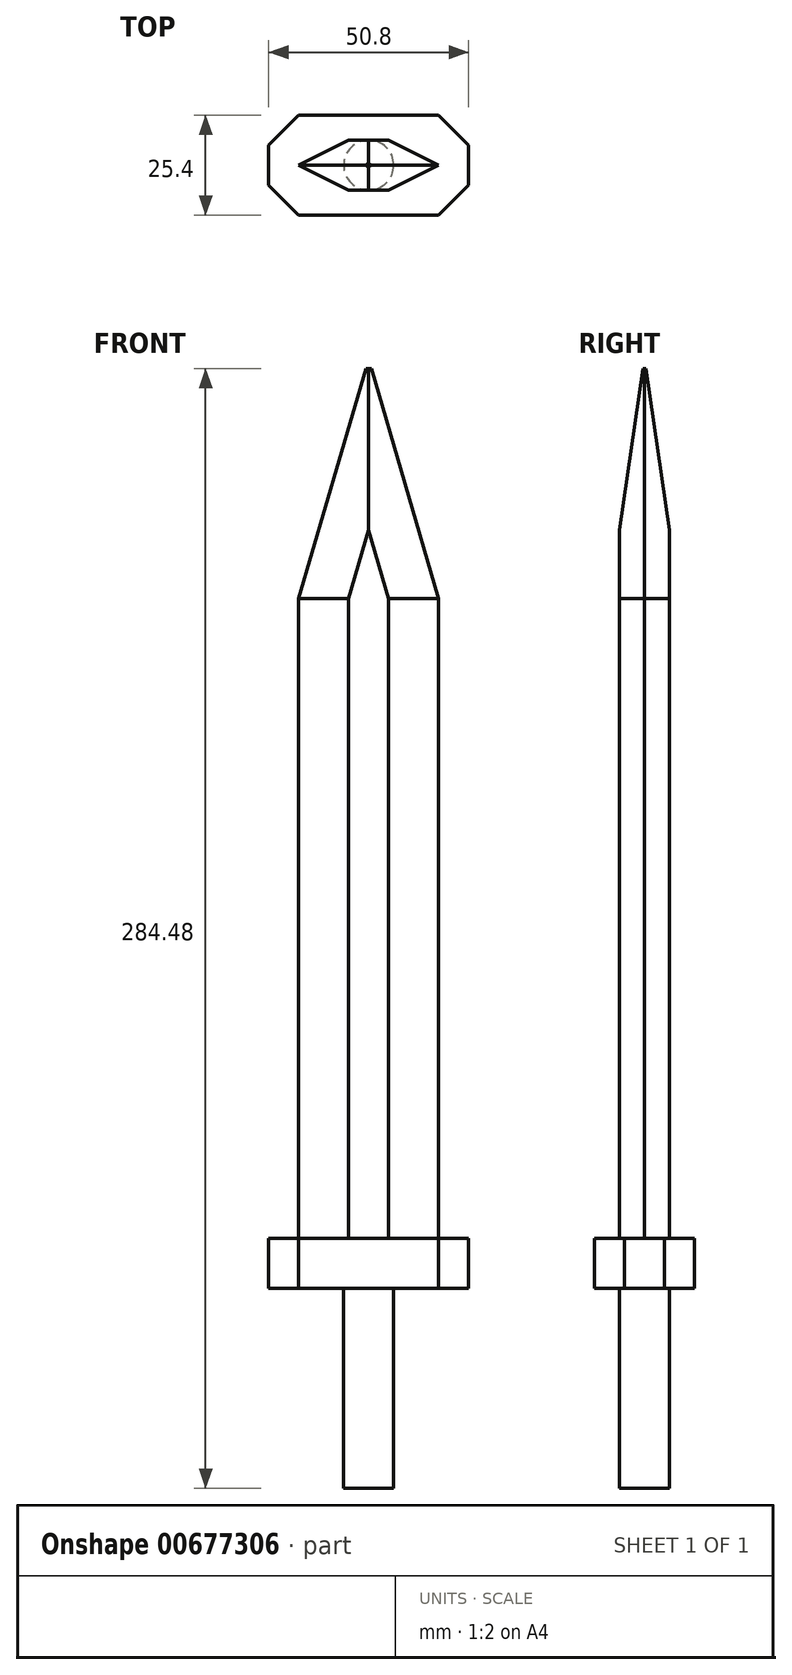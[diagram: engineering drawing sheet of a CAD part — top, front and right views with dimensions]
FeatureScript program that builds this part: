
annotation { "Feature Type Name" : "Feature", "Feature Type Description" : "" }
export const myFeature = defineFeature(function(context is Context, id is Id, definition is map)
    precondition{}
    {
        {
            var Q0;
            Q0=qCreatedBy(makeId("Top.planeOp"),FACE);
            var sketch = newSketch(context, id + "F0", { "sketchPlane" : qUnion([Q0])});
            skLineSegment(sketch, "E0.bottom", {"start": v(-25.4, 12.7) * mm, "end": v(25.4, 12.7) * mm});
            skLineSegment(sketch, "E0.top", {"start": v(-25.4, -12.7) * mm, "end": v(25.4, -12.7) * mm});
            skLineSegment(sketch, "E0.left", {"start": v(-25.4, 12.7) * mm, "end": v(-25.4, -12.7) * mm});
            skLineSegment(sketch, "E0.right", {"start": v(25.4, 12.7) * mm, "end": v(25.4, -12.7) * mm});
            skSolve(sketch);
        }
        {
            var Q0;
            Q0 = qSketchRegion(id + "F0", true);
            extrude(context, id + "F1", {"entities" : qUnion([Q0]), "depth" : 12.7 * mm, "offsetDistance" : 25.4 * mm});
        }
        {
            var Q0;
            Q0=makeQuery(id+"F1.opExtrude","CAP_FACE",FACE,{"disambiguationData":[OSD([sQuery(id+"F0.wireOp",EDGE,"E0.bottom"),sQuery(id+"F0.wireOp",EDGE,"E0.top"),sQuery(id+"F0.wireOp",EDGE,"E0.left"),sQuery(id+"F0.wireOp",EDGE,"E0.right")])],"isStart":true});
            var sketch = newSketch(context, id + "F2", { "sketchPlane" : qUnion([Q0])});
            skCircle(sketch, "E1", {"center": v(0, 0) * mm, "radius": 6.35 * mm});
            skSolve(sketch);
        }
        {
            var Q0;
            Q0=makeQuery(id+"F2.imprint","IMPRINT",FACE,{"disambiguationData":[TD([[makeQuery(id+"F2.imprint","IMPRINT",EDGE,{"derivedFrom":sQuery(id+"F2.wireOp",EDGE,"E1")}),1.0]])]});
            extrude(context, id + "F3", {"entities" : qUnion([Q0]), "operationType" : NewBodyOperationType.ADD, "depth" : 50.8 * mm, "offsetDistance" : 25.4 * mm});
        }
        {
            var Q0;
            Q0=makeQuery(id+"F1.opExtrude","CAP_FACE",FACE,{"disambiguationData":[OSD([sQuery(id+"F0.wireOp",EDGE,"E0.bottom"),sQuery(id+"F0.wireOp",EDGE,"E0.top"),sQuery(id+"F0.wireOp",EDGE,"E0.left"),sQuery(id+"F0.wireOp",EDGE,"E0.right")])],"isStart":false});
            var sketch = newSketch(context, id + "F4", { "sketchPlane" : qUnion([Q0])});
            skLineSegment(sketch, "E2.bottom", {"start": v(-17.78, -6.35) * mm, "end": v(17.78, -6.35) * mm});
            skLineSegment(sketch, "E2.top", {"start": v(-17.78, 6.35) * mm, "end": v(17.78, 6.35) * mm});
            skLineSegment(sketch, "E2.left", {"start": v(-17.78, -6.35) * mm, "end": v(-17.78, 6.35) * mm});
            skLineSegment(sketch, "E2.right", {"start": v(17.78, -6.35) * mm, "end": v(17.78, 6.35) * mm});
            skSolve(sketch);
        }
        {
            var Q0;
            Q0 = qSketchRegion(id + "F4", true);
            extrude(context, id + "F5", {"entities" : qUnion([Q0]), "operationType" : NewBodyOperationType.ADD, "depth" : 220.98 * mm, "offsetDistance" : 25.4 * mm});
        }
        {
            var Q0;
            Q0=makeQuery(id+"F5.opExtrude","SWEPT_EDGE",EDGE,{"disambiguationData":[OSD([sQuery(id+"F4.wireOp",EDGE,"E2.bottom"),sQuery(id+"F4.wireOp",EDGE,"E2.right")])]});
            var Q1;
            Q1=makeQuery(id+"F5.opExtrude","SWEPT_EDGE",EDGE,{"disambiguationData":[OSD([sQuery(id+"F4.wireOp",EDGE,"E2.top"),sQuery(id+"F4.wireOp",EDGE,"E2.right")])]});
            var Q2;
            Q2=makeQuery(id+"F5.opExtrude","SWEPT_EDGE",EDGE,{"disambiguationData":[OSD([sQuery(id+"F4.wireOp",EDGE,"E2.top"),sQuery(id+"F4.wireOp",EDGE,"E2.left")])]});
            var Q3;
            Q3=makeQuery(id+"F5.opExtrude","SWEPT_EDGE",EDGE,{"disambiguationData":[OSD([sQuery(id+"F4.wireOp",EDGE,"E2.bottom"),sQuery(id+"F4.wireOp",EDGE,"E2.left")])]});
            chamfer(context, id + "F6", {"entities" : qUnion([Q0, Q1, Q2, Q3]), "chamferType" : ChamferType.TWO_OFFSETS, "width1" : 6.35 * mm, "oppositeDirection" : false, "width2" : 12.7 * mm, "tangentPropagation" : true});
        }
        {
            var Q0;
            {var subQ0=sQuery(id+"F4.wireOp",EDGE,"E2.right");var subQ1=sQuery(id+"F4.wireOp",EDGE,"E2.top");Q0=makeQuery(id+"F6.opChamfer","BLEND_EDGE",EDGE,{"blendedFrom":[makeQuery(id+"F5.opExtrude","SWEPT_EDGE",EDGE,{"disambiguationData":[OSD([subQ1,subQ0])]}),makeQuery(id+"F5.opExtrude","CAP_FACE",FACE,{"disambiguationData":[OSD([sQuery(id+"F4.wireOp",EDGE,"E2.bottom"),subQ1,sQuery(id+"F4.wireOp",EDGE,"E2.left"),subQ0])],"isStart":false})],"blendedInto":[makeQuery(id+"F5.opExtrude","CAP_FACE",FACE,{"disambiguationData":[OSD([sQuery(id+"F4.wireOp",EDGE,"E2.bottom"),subQ1,sQuery(id+"F4.wireOp",EDGE,"E2.left"),subQ0])],"isStart":false})]});}
            var Q1;
            {var subQ0=sQuery(id+"F4.wireOp",EDGE,"E2.right");var subQ1=sQuery(id+"F4.wireOp",EDGE,"E2.bottom");Q1=makeQuery(id+"F6.opChamfer","BLEND_EDGE",EDGE,{"blendedFrom":[makeQuery(id+"F5.opExtrude","SWEPT_EDGE",EDGE,{"disambiguationData":[OSD([subQ1,subQ0])]}),makeQuery(id+"F5.opExtrude","CAP_FACE",FACE,{"disambiguationData":[OSD([subQ1,sQuery(id+"F4.wireOp",EDGE,"E2.top"),sQuery(id+"F4.wireOp",EDGE,"E2.left"),subQ0])],"isStart":false})],"blendedInto":[makeQuery(id+"F5.opExtrude","CAP_FACE",FACE,{"disambiguationData":[OSD([subQ1,sQuery(id+"F4.wireOp",EDGE,"E2.top"),sQuery(id+"F4.wireOp",EDGE,"E2.left"),subQ0])],"isStart":false})]});}
            var Q2;
            {var subQ0=sQuery(id+"F4.wireOp",EDGE,"E2.left");var subQ1=sQuery(id+"F4.wireOp",EDGE,"E2.bottom");Q2=makeQuery(id+"F6.opChamfer","BLEND_EDGE",EDGE,{"blendedFrom":[makeQuery(id+"F5.opExtrude","SWEPT_EDGE",EDGE,{"disambiguationData":[OSD([subQ1,subQ0])]}),makeQuery(id+"F5.opExtrude","CAP_FACE",FACE,{"disambiguationData":[OSD([subQ1,sQuery(id+"F4.wireOp",EDGE,"E2.top"),subQ0,sQuery(id+"F4.wireOp",EDGE,"E2.right")])],"isStart":false})],"blendedInto":[makeQuery(id+"F5.opExtrude","CAP_FACE",FACE,{"disambiguationData":[OSD([subQ1,sQuery(id+"F4.wireOp",EDGE,"E2.top"),subQ0,sQuery(id+"F4.wireOp",EDGE,"E2.right")])],"isStart":false})]});}
            var Q3;
            {var subQ0=sQuery(id+"F4.wireOp",EDGE,"E2.left");var subQ1=sQuery(id+"F4.wireOp",EDGE,"E2.top");Q3=makeQuery(id+"F6.opChamfer","BLEND_EDGE",EDGE,{"blendedFrom":[makeQuery(id+"F5.opExtrude","SWEPT_EDGE",EDGE,{"disambiguationData":[OSD([subQ1,subQ0])]}),makeQuery(id+"F5.opExtrude","CAP_FACE",FACE,{"disambiguationData":[OSD([sQuery(id+"F4.wireOp",EDGE,"E2.bottom"),subQ1,subQ0,sQuery(id+"F4.wireOp",EDGE,"E2.right")])],"isStart":false})],"blendedInto":[makeQuery(id+"F5.opExtrude","CAP_FACE",FACE,{"disambiguationData":[OSD([sQuery(id+"F4.wireOp",EDGE,"E2.bottom"),subQ1,subQ0,sQuery(id+"F4.wireOp",EDGE,"E2.right")])],"isStart":false})]});}
            chamfer(context, id + "F7", {"entities" : qUnion([Q0, Q1, Q2, Q3]), "chamferType" : ChamferType.TWO_OFFSETS, "width1" : 7.62 * mm, "oppositeDirection" : false, "width2" : 58.42 * mm, "tangentPropagation" : true});
        }
        {
            var Q0;
            Q0=makeQuery(id+"F1.opExtrude","SWEPT_EDGE",EDGE,{"disambiguationData":[OSD([sQuery(id+"F0.wireOp",EDGE,"E0.top"),sQuery(id+"F0.wireOp",EDGE,"E0.left")])]});
            var Q1;
            Q1=makeQuery(id+"F1.opExtrude","SWEPT_EDGE",EDGE,{"disambiguationData":[OSD([sQuery(id+"F0.wireOp",EDGE,"E0.top"),sQuery(id+"F0.wireOp",EDGE,"E0.right")])]});
            var Q2;
            Q2=makeQuery(id+"F1.opExtrude","SWEPT_EDGE",EDGE,{"disambiguationData":[OSD([sQuery(id+"F0.wireOp",EDGE,"E0.bottom"),sQuery(id+"F0.wireOp",EDGE,"E0.right")])]});
            var Q3;
            Q3=makeQuery(id+"F1.opExtrude","SWEPT_EDGE",EDGE,{"disambiguationData":[OSD([sQuery(id+"F0.wireOp",EDGE,"E0.bottom"),sQuery(id+"F0.wireOp",EDGE,"E0.left")])]});
            chamfer(context, id + "F8", {"entities" : qUnion([Q0, Q1, Q2, Q3]), "chamferType" : ChamferType.TWO_OFFSETS, "width1" : 7.62 * mm, "oppositeDirection" : false, "width2" : 7.62 * mm, "tangentPropagation" : true});
        }
    });
